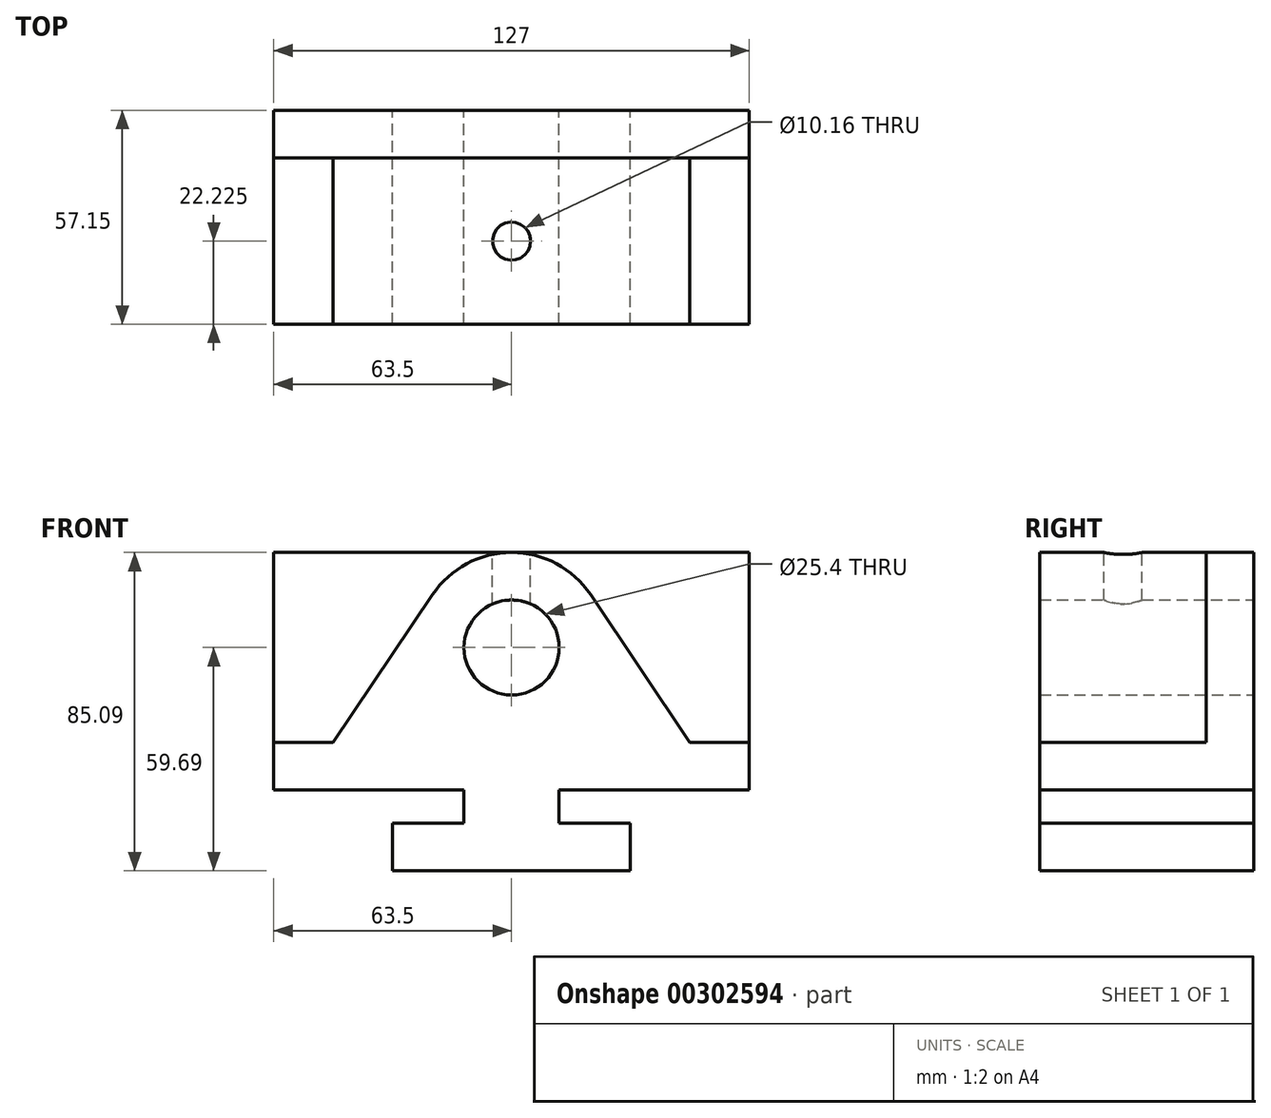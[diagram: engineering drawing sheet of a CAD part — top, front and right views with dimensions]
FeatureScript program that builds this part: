
annotation { "Feature Type Name" : "Feature", "Feature Type Description" : "" }
export const myFeature = defineFeature(function(context is Context, id is Id, definition is map)
    precondition{}
    {
        {
            var Q0;
            Q0=qCreatedBy(makeId("Front.planeOp"),FACE);
            var sketch = newSketch(context, id + "F0", { "sketchPlane" : qUnion([Q0])});
            skLineSegment(sketch, "E0", {"start": v(-31.75, 0) * mm, "end": v(31.75, 0) * mm});
            skLineSegment(sketch, "E1", {"start": v(31.75, 0) * mm, "end": v(31.75, 12.7) * mm});
            skLineSegment(sketch, "E2", {"start": v(31.75, 12.7) * mm, "end": v(12.7, 12.7) * mm});
            skLineSegment(sketch, "E3", {"start": v(12.7, 12.7) * mm, "end": v(12.7, 21.6) * mm});
            skLineSegment(sketch, "E4", {"start": v(12.7, 21.59) * mm, "end": v(63.5, 21.59) * mm});
            skLineSegment(sketch, "E5", {"start": v(63.5, 21.59) * mm, "end": v(63.5, 85.1) * mm});
            skLineSegment(sketch, "E6", {"start": v(63.5, 85.1) * mm, "end": v(-63.5, 85.1) * mm});
            skLineSegment(sketch, "E7", {"start": v(-63.5, 85.1) * mm, "end": v(-63.5, 21.59) * mm});
            skLineSegment(sketch, "E8", {"start": v(-63.5, 21.59) * mm, "end": v(-12.7, 21.6) * mm});
            skLineSegment(sketch, "E9", {"start": v(-12.7, 21.6) * mm, "end": v(-12.7, 12.7) * mm});
            skLineSegment(sketch, "E10", {"start": v(-12.7, 12.7) * mm, "end": v(-31.75, 12.7) * mm});
            skLineSegment(sketch, "E11", {"start": v(-31.75, 12.7) * mm, "end": v(-31.75, 0) * mm});
            skLineSegment(sketch, "E12", {"start": v(0, 0) * mm, "end": v(0, 85.1) * mm, "construction": true});
            skLineSegment(sketch, "E13", {"start": v(63.5, 21.59) * mm, "end": v(63.5, 34.3) * mm});
            skLineSegment(sketch, "E14", {"start": v(63.5, 34.3) * mm, "end": v(47.63, 34.3) * mm});
            skLineSegment(sketch, "E15", {"start": v(47.63, 34.3) * mm, "end": v(21.1, 73.84) * mm});
            skLineSegment(sketch, "E16", {"start": v(-63.5, 21.59) * mm, "end": v(-63.5, 34.3) * mm});
            skLineSegment(sketch, "E17", {"start": v(-63.5, 34.29) * mm, "end": v(-47.63, 34.29) * mm});
            skLineSegment(sketch, "E18", {"start": v(-47.62, 34.29) * mm, "end": v(-21.1, 73.84) * mm});
            skArc(sketch, "E19", {"start": v(-21.1, 73.84) * mm, "mid": v(0, 85.1) * mm, "end": v(21.1, 73.84) * mm});
            skCircle(sketch, "E20", {"center": v(0, 59.7) * mm, "radius": 12.7 * mm});
            skSolve(sketch);
        }
        {
            var Q0;
            Q0=makeQuery(id+"F0.imprint","IMPRINT",FACE,{"disambiguationData":[TD([[makeQuery(id+"F0.imprint","IMPRINT",EDGE,{"derivedFrom":sQuery(id+"F0.wireOp",EDGE,"E0")}),1.0]])]});
            extrude(context, id + "F1", {"entities" : qUnion([Q0]), "depth" : 44.45 * mm});
        }
        {
            var Q0;
            {var subQ1=sQuery(id+"F0.wireOp",EDGE,"E5");Q0=makeQuery(id+"F0.imprint","IMPRINT",FACE,{"disambiguationData":[TD([[makeQuery(id+"F0.imprint","IMPRINT",EDGE,{"derivedFrom":subQ1}),1.0]])]});}
            var Q1;
            {var subQ1=sQuery(id+"F0.wireOp",EDGE,"E7");Q1=makeQuery(id+"F0.imprint","IMPRINT",FACE,{"disambiguationData":[TD([[makeQuery(id+"F0.imprint","IMPRINT",EDGE,{"derivedFrom":subQ1}),1.0]])]});}
            var Q2;
            Q2=makeQuery(id+"F0.imprint","IMPRINT",FACE,{"disambiguationData":[TD([[makeQuery(id+"F0.imprint","IMPRINT",EDGE,{"derivedFrom":sQuery(id+"F0.wireOp",EDGE,"E0")}),1.0]])]});
            extrude(context, id + "F2", {"entities" : qUnion([Q0, Q1, Q2]), "operationType" : NewBodyOperationType.ADD, "oppositeDirection" : true, "depth" : 12.7 * mm});
        }
        {
            var Q0;
            Q0=makeQuery(id+"F2.opExtrude","SWEPT_FACE",FACE,{"disambiguationData":[OSD([sQuery(id+"F0.wireOp",EDGE,"E6")])]});
            var sketch = newSketch(context, id + "F3", { "sketchPlane" : qUnion([Q0])});
            skLineSegment(sketch, "E21.0.0", {"start": v(0, 0) * mm, "end": v(-21.1, 0) * mm});
            skLineSegment(sketch, "E21.0.1", {"start": v(-21.1, 0) * mm, "end": v(-21.1, -44.45) * mm});
            skLineSegment(sketch, "E21.0.2", {"start": v(-21.1, -44.45) * mm, "end": v(21.1, -44.45) * mm});
            skLineSegment(sketch, "E21.0.3", {"start": v(21.1, -44.45) * mm, "end": v(21.1, 0) * mm});
            skLineSegment(sketch, "E21.0.4", {"start": v(21.1, 0) * mm, "end": v(0, 0) * mm});
            skLineSegment(sketch, "E22.0.0", {"start": v(0, 0) * mm, "end": v(63.5, 0) * mm});
            skLineSegment(sketch, "E22.0.1", {"start": v(63.5, 0) * mm, "end": v(63.5, 12.7) * mm});
            skLineSegment(sketch, "E22.0.2", {"start": v(63.5, 12.7) * mm, "end": v(-63.5, 12.7) * mm});
            skLineSegment(sketch, "E22.0.3", {"start": v(-63.5, 12.7) * mm, "end": v(-63.5, 0) * mm});
            skLineSegment(sketch, "E22.0.4", {"start": v(-63.5, 0) * mm, "end": v(0, 0) * mm});
            skCircle(sketch, "E23", {"center": v(0, -22.23) * mm, "radius": 5.08 * mm});
            skLineSegment(sketch, "E24", {"start": v(0, 0) * mm, "end": v(0, -22.23) * mm, "construction": true});
            skSolve(sketch);
        }
        {
            var Q0;
            Q0=makeQuery(id+"F3.imprint","IMPRINT",FACE,{"disambiguationData":[TD([[makeQuery(id+"F3.imprint","IMPRINT",EDGE,{"derivedFrom":sQuery(id+"F3.wireOp",EDGE,"E23")}),1.0]])]});
            extrude(context, id + "F4", {"entities" : qUnion([Q0]), "operationType" : NewBodyOperationType.REMOVE, "oppositeDirection" : true, "depth" : 25.4 * mm});
        }
    });
